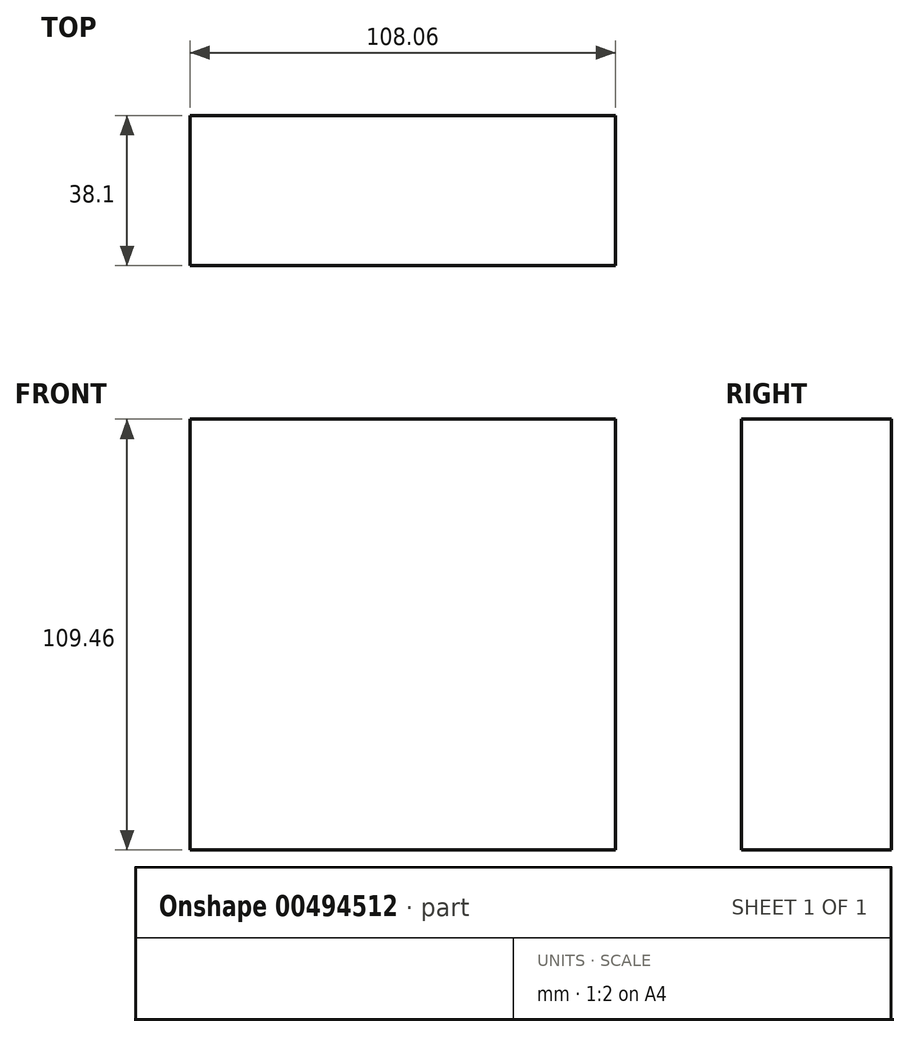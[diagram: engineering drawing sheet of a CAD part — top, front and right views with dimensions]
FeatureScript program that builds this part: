
annotation { "Feature Type Name" : "Feature", "Feature Type Description" : "" }
export const myFeature = defineFeature(function(context is Context, id is Id, definition is map)
    precondition{}
    {
        {
            var Q0;
            Q0=qCreatedBy(makeId("Front.planeOp"),FACE);
            var sketch = newSketch(context, id + "F0", { "sketchPlane" : qUnion([Q0])});
            skLineSegment(sketch, "E0.bottom", {"start": v(54.03, 54.73) * mm, "end": v(-54.03, 54.73) * mm});
            skLineSegment(sketch, "E0.top", {"start": v(54.03, -54.73) * mm, "end": v(-54.03, -54.73) * mm});
            skLineSegment(sketch, "E0.left", {"start": v(54.03, 54.73) * mm, "end": v(54.03, -54.73) * mm});
            skLineSegment(sketch, "E0.right", {"start": v(-54.03, 54.73) * mm, "end": v(-54.03, -54.73) * mm});
            skPoint(sketch, "E0.middle", {"position": v(0, 0) * mm});
            skSolve(sketch);
        }
        {
            var Q0;
            Q0=makeQuery(id+"F0.imprint","IMPRINT",FACE,{"disambiguationData":[TD([[makeQuery(id+"F0.imprint","IMPRINT",EDGE,{"derivedFrom":sQuery(id+"F0.wireOp",EDGE,"E0.bottom")}),1.0]])]});
            extrude(context, id + "F1", {"entities" : qUnion([Q0]), "depth" : 38.1 * mm});
        }
    });
